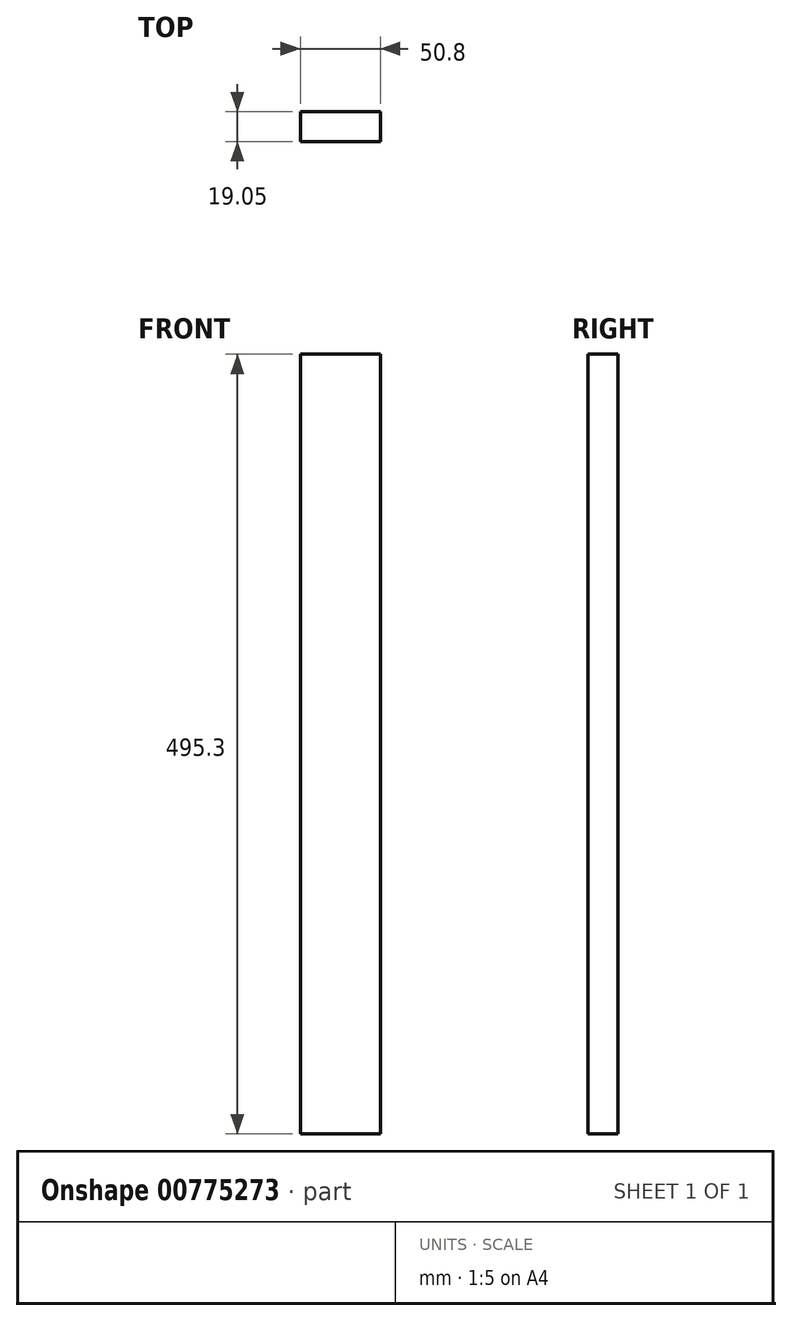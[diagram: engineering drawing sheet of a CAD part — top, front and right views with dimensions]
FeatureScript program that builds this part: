
annotation { "Feature Type Name" : "Feature", "Feature Type Description" : "" }
export const myFeature = defineFeature(function(context is Context, id is Id, definition is map)
    precondition{}
    {
        {
            var Q0;
            Q0=qCreatedBy(makeId("Front.planeOp"),FACE);
            var sketch = newSketch(context, id + "F0", { "sketchPlane" : qUnion([Q0])});
            skLineSegment(sketch, "E0.bottom", {"start": v(0, 0) * mm, "end": v(-50.8, 0) * mm});
            skLineSegment(sketch, "E0.top", {"start": v(0, 495.3) * mm, "end": v(-50.8, 495.3) * mm});
            skLineSegment(sketch, "E0.left", {"start": v(0, 0) * mm, "end": v(0, 495.3) * mm});
            skLineSegment(sketch, "E0.right", {"start": v(-50.8, 0) * mm, "end": v(-50.8, 495.3) * mm});
            skSolve(sketch);
        }
        {
            var Q0;
            Q0 = qSketchRegion(id + "F0", true);
            extrude(context, id + "F1", {"entities" : qUnion([Q0]), "depth" : 19.05 * mm, "offsetDistance" : 25.4 * mm});
        }
    });
